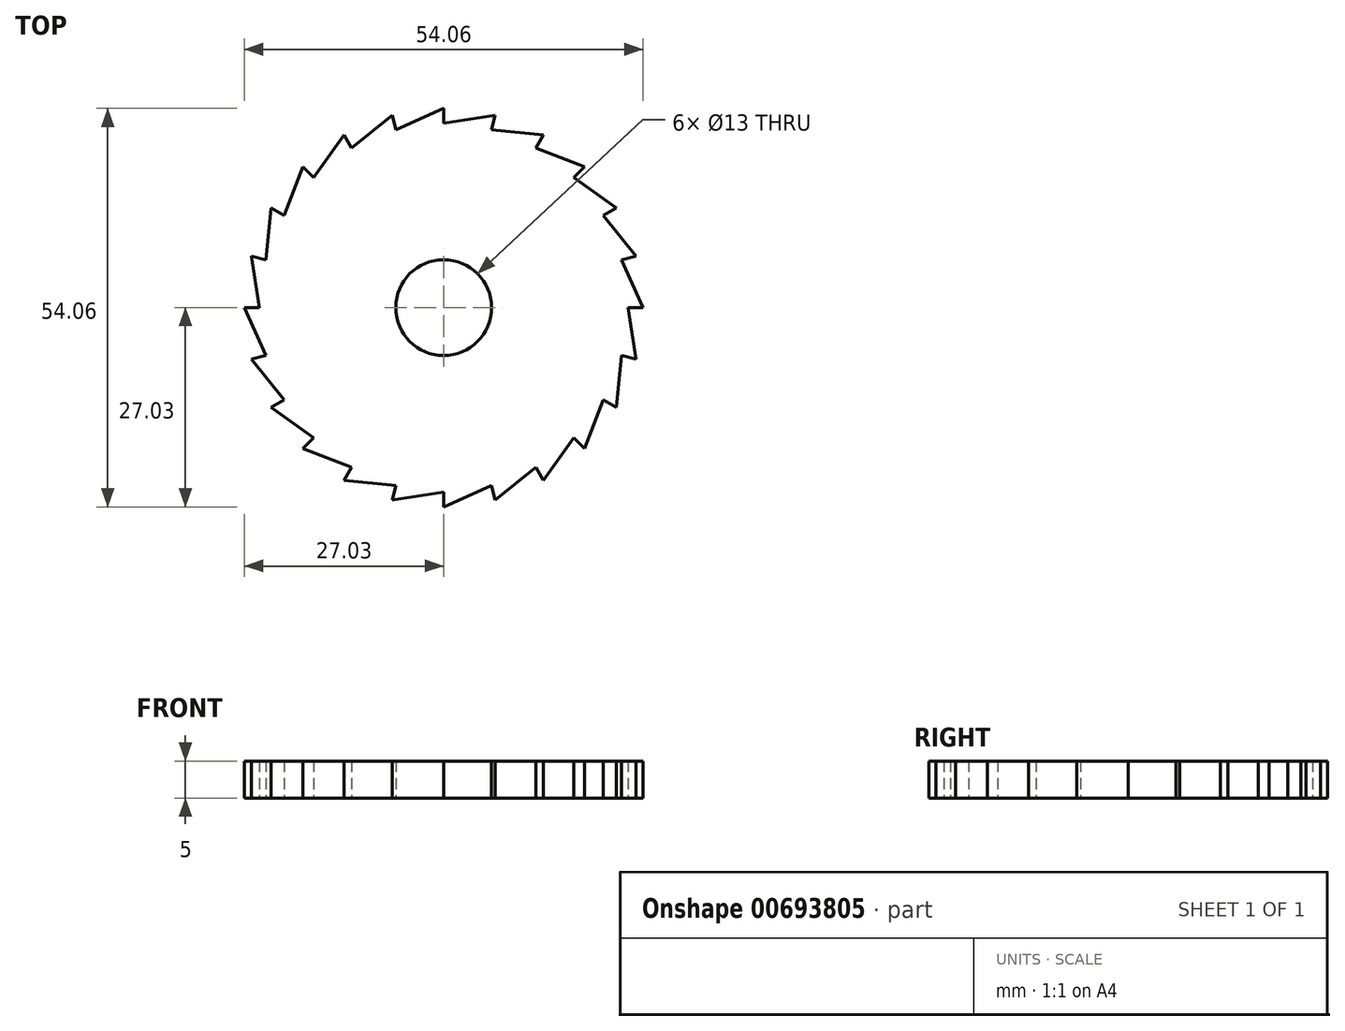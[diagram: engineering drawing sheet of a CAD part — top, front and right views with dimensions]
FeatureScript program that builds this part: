
annotation { "Feature Type Name" : "Feature", "Feature Type Description" : "" }
export const myFeature = defineFeature(function(context is Context, id is Id, definition is map)
    precondition{}
    {
        {
            var Q0;
            Q0=qCreatedBy(makeId("Top.planeOp"),FACE);
            var sketch = newSketch(context, id + "F0", { "sketchPlane" : qUnion([Q0])});
            skLineSegment(sketch, "E0", {"start": v(0, 25) * mm, "end": v(7, 26.1) * mm});
            skLineSegment(sketch, "E1", {"start": v(7, 26.1) * mm, "end": v(6.47, 24.15) * mm});
            skLineSegment(sketch, "E2.1.0", {"start": v(13.51, 23.4) * mm, "end": v(12.5, 21.65) * mm});
            skLineSegment(sketch, "E2.1.1", {"start": v(6.47, 24.15) * mm, "end": v(13.51, 23.4) * mm});
            skLineSegment(sketch, "E2.2.0", {"start": v(19.11, 19.11) * mm, "end": v(17.68, 17.68) * mm});
            skLineSegment(sketch, "E2.2.1", {"start": v(12.5, 21.65) * mm, "end": v(19.11, 19.11) * mm});
            skLineSegment(sketch, "E2.3.0", {"start": v(23.4, 13.51) * mm, "end": v(21.65, 12.5) * mm});
            skLineSegment(sketch, "E2.3.1", {"start": v(17.68, 17.68) * mm, "end": v(23.4, 13.51) * mm});
            skLineSegment(sketch, "E2.4.0", {"start": v(26.1, 7) * mm, "end": v(24.15, 6.47) * mm});
            skLineSegment(sketch, "E2.4.1", {"start": v(21.65, 12.5) * mm, "end": v(26.1, 7) * mm});
            skLineSegment(sketch, "E2.5.0", {"start": v(27.03, 0) * mm, "end": v(25, 0) * mm});
            skLineSegment(sketch, "E2.5.1", {"start": v(24.15, 6.47) * mm, "end": v(27.03, 0) * mm});
            skPoint(sketch, "E2.center", {"position": v(0, 0) * mm});
            skLineSegment(sketch, "E2.anchor1", {"start": v(0, 0) * mm, "end": v(0, 25) * mm, "construction": true});
            skLineSegment(sketch, "E2.anchor2", {"start": v(0, 0) * mm, "end": v(24.15, 6.47) * mm, "construction": true});
            skLineSegment(sketch, "E3.1.0", {"start": v(25, 0) * mm, "end": v(26.1, -7) * mm});
            skLineSegment(sketch, "E3.1.1", {"start": v(26.1, -7) * mm, "end": v(24.15, -6.47) * mm});
            skLineSegment(sketch, "E3.2.0", {"start": v(24.15, -6.47) * mm, "end": v(23.4, -13.51) * mm});
            skLineSegment(sketch, "E3.2.1", {"start": v(23.4, -13.51) * mm, "end": v(21.65, -12.5) * mm});
            skLineSegment(sketch, "E3.3.0", {"start": v(21.65, -12.5) * mm, "end": v(19.11, -19.11) * mm});
            skLineSegment(sketch, "E3.3.1", {"start": v(19.11, -19.11) * mm, "end": v(17.68, -17.68) * mm});
            skLineSegment(sketch, "E3.4.0", {"start": v(17.68, -17.68) * mm, "end": v(13.51, -23.4) * mm});
            skLineSegment(sketch, "E3.4.1", {"start": v(13.51, -23.4) * mm, "end": v(12.5, -21.65) * mm});
            skLineSegment(sketch, "E3.5.0", {"start": v(12.5, -21.65) * mm, "end": v(7, -26.1) * mm});
            skLineSegment(sketch, "E3.5.1", {"start": v(7, -26.1) * mm, "end": v(6.47, -24.15) * mm});
            skLineSegment(sketch, "E3.anchor1", {"start": v(0, 0) * mm, "end": v(25, 0) * mm, "construction": true});
            skLineSegment(sketch, "E3.anchor2", {"start": v(0, 0) * mm, "end": v(6.47, -24.15) * mm, "construction": true});
            skLineSegment(sketch, "E4.1.0", {"start": v(6.47, -24.15) * mm, "end": v(0, -27.03) * mm});
            skLineSegment(sketch, "E4.1.1", {"start": v(0, -27.03) * mm, "end": v(0, -25) * mm});
            skLineSegment(sketch, "E4.2.0", {"start": v(0, -25) * mm, "end": v(-7, -26.1) * mm});
            skLineSegment(sketch, "E4.2.1", {"start": v(-7, -26.1) * mm, "end": v(-6.47, -24.15) * mm});
            skLineSegment(sketch, "E4.3.0", {"start": v(-6.47, -24.15) * mm, "end": v(-13.51, -23.4) * mm});
            skLineSegment(sketch, "E4.3.1", {"start": v(-13.51, -23.4) * mm, "end": v(-12.5, -21.65) * mm});
            skLineSegment(sketch, "E4.4.0", {"start": v(-12.5, -21.65) * mm, "end": v(-19.11, -19.11) * mm});
            skLineSegment(sketch, "E4.4.1", {"start": v(-19.11, -19.11) * mm, "end": v(-17.68, -17.68) * mm});
            skLineSegment(sketch, "E4.5.0", {"start": v(-17.68, -17.68) * mm, "end": v(-23.4, -13.51) * mm});
            skLineSegment(sketch, "E4.5.1", {"start": v(-23.4, -13.51) * mm, "end": v(-21.65, -12.5) * mm});
            skLineSegment(sketch, "E4.anchor1", {"start": v(0, 0) * mm, "end": v(7, -26.1) * mm, "construction": true});
            skLineSegment(sketch, "E5.1.0", {"start": v(-21.65, -12.5) * mm, "end": v(-26.1, -7) * mm});
            skLineSegment(sketch, "E5.1.1", {"start": v(-26.1, -7) * mm, "end": v(-24.15, -6.47) * mm});
            skLineSegment(sketch, "E5.2.0", {"start": v(-24.15, -6.47) * mm, "end": v(-27.03, 0) * mm});
            skLineSegment(sketch, "E5.2.1", {"start": v(-27.03, 0) * mm, "end": v(-25, 0) * mm});
            skLineSegment(sketch, "E5.3.0", {"start": v(-25, 0) * mm, "end": v(-26.1, 7) * mm});
            skLineSegment(sketch, "E5.3.1", {"start": v(-26.1, 7) * mm, "end": v(-24.15, 6.47) * mm});
            skLineSegment(sketch, "E5.4.0", {"start": v(-24.15, 6.47) * mm, "end": v(-23.4, 13.51) * mm});
            skLineSegment(sketch, "E5.4.1", {"start": v(-23.4, 13.51) * mm, "end": v(-21.65, 12.5) * mm});
            skLineSegment(sketch, "E5.5.0", {"start": v(-21.65, 12.5) * mm, "end": v(-19.11, 19.11) * mm});
            skLineSegment(sketch, "E5.5.1", {"start": v(-19.11, 19.11) * mm, "end": v(-17.68, 17.68) * mm});
            skLineSegment(sketch, "E5.anchor1", {"start": v(0, 0) * mm, "end": v(-23.4, -13.51) * mm, "construction": true});
            skLineSegment(sketch, "E6.1.0", {"start": v(-13.51, 23.4) * mm, "end": v(-12.5, 21.65) * mm});
            skLineSegment(sketch, "E6.1.1", {"start": v(-17.68, 17.68) * mm, "end": v(-13.51, 23.4) * mm});
            skLineSegment(sketch, "E6.2.0", {"start": v(-7, 26.1) * mm, "end": v(-6.47, 24.15) * mm});
            skLineSegment(sketch, "E6.2.1", {"start": v(-12.5, 21.65) * mm, "end": v(-7, 26.1) * mm});
            skLineSegment(sketch, "E6.3.0", {"start": v(0, 27.03) * mm, "end": v(0, 25) * mm});
            skLineSegment(sketch, "E6.3.1", {"start": v(-6.47, 24.15) * mm, "end": v(0, 27.03) * mm});
            skLineSegment(sketch, "E6.anchor1", {"start": v(0, 0) * mm, "end": v(-17.68, 17.68) * mm, "construction": true});
            skCircle(sketch, "E7", {"center": v(0, 0) * mm, "radius": 6.5 * mm});
            skSolve(sketch);
        }
        {
            var Q0;
            Q0 = qSketchRegion(id + "F0", true);
            extrude(context, id + "F1", {"entities" : qUnion([Q0]), "depth" : 5 * mm, "offsetDistance" : 25 * mm});
        }
    });
